# Revit family: Lavatory-TOTO-Commercial-LT308
name_source: partatom
category: Plumbing Fixtures
revit_build: Autodesk Revit Architecture 2013 (Build: 20130531_2115(x64)
units: mm (PartAtom-declared; Revit-internal decimal feet)

## types (1)
- Lt 308
    04 CSI = 22 42 16
    95 CSI = 15410
    ADA Compliant = Yes
    Assembly Code = D2010310
    Basin Depth = 1' - 2 3/4"
    Basin Diameter = 0' - 0"
    Basin Width = 1' - 3 1/8"
    CAD Drawing URL = http://assets.totousa.com
    Certifications = IAPMO(cUPC), State of Massachusetts , City of Los Angeles, and others
    Code Compliance = UPC, IPC, NSPC, NPC Canada,and others
    Cold Water Connection Radius = 0' - 0 3/8"
    Cold Water Connector = Cold Water Connection
    Color Availability = Standard,#01 Cotton,#03 Bone,#12 Sedona Beige
    Default Elevation = 4' - 0"
    Depth = 2' - 3"
    Description = Commercial Wall-Mount Wheelchair User's Lavatory - ADA
    Finish = Vitreous China - TOTO - 01 Cotton
    Height = 0' - 0"
    Hot Water Connection Radius = 0' - 0 3/8"
    Hot Water Connector = Hot Water Connection
    Industry Standards = Meets and exceeds ASME A112.19.2/CSA B45.1,
    Manufacturer = TOTO USA, Inc.
    Manufacturer Fax = (770) 282-0002
    Material = Vitreous china
    Model = LT308
    Mounting = wall-mount
    Sanitary Connector = Sanitary Connection
    SanoGloss Available = No
    Series = Commercial
    Shipping Weight = 56.00 lb
    Sink Configuration = Single Sink
    Sink Type = Lavatory
    Spec Sheet URL = http://assets.totousa.com
    Style = Commercial
    Subcategory = Lavatories
    Toto BIM Number = BM-00376
    URL = http://www.totousa.com
    Warranty = One Year Limited Warranty
    Warranty URL = http://www.totousa.com
    Waste Connection NPT Radius = 0' - 0 5/8"
    Width = 1' - 8 1/2"
    ecoScorecard Product Page = http://toto.ecoscorecard.com
    ecoScorecard_data = http://toto.ecoscorecard.com

## geometry (parser evidence)
native form markers: Blend x12, Sweep x3
no freeform markers — native parametric forms only
